# Revit family: Emergency_Equipment-Tepid-Floor_Mounted_Eye_Face_Wash-S2510
name_source: partatom
category: Plumbing Fixtures
revit_build: Autodesk Revit Architecture 2016 (Build: 20150220_1215(x64)
units: mm (PartAtom-declared; Revit-internal decimal feet)

## family parameters
Always vertical = Yes
Cut with Voids When Loaded = No
OmniClass Number = 23.45.05.14.24
OmniClass Title = Eye Wash Fountains
Part Type = Normal
Room Calculation Point = No
Round Connector Dimension = Use Diameter
Shared = No
Work Plane-Based = No

## types (12) — shared parameters
C Pipe length = 0' - 1 3/4"
CW Connection = Yes
Description = Floor Mounted Eye-Face Wash
Dimension Disclaimer = Dimensions are ±0.50”. Design and specifications are subject to change without notice.
Drain Connection = 1"
HW Connection = Yes
Height = 3' - 2 5/16"
Length = 1' - 8 1/2"
Manufacturer = Stingray Systems
Product Documentation Link = http://www.tepid.com
Product Name = Floor Mounted Standard Eye-Face Wash
Product Page URL = http://www.tepid.com
Supply Connection = 1"
URL = www.tepid.com
Vent Connection = No
Version = 2016-v1.0a
Waste Connection = Yes

## per-type parameters (varying)
| type | AB Bowl | Base Finish | Bowl Material | Filter | Pipe Finish | SS Bowl | Width |
| S2510-SS-NFT-SSNA | No | Metal - Stingray - Stainless Steel SS | Metal - Stingray - Stainless Steel SS | No | Metal - Stingray - Stainless Steel SS | Yes | 1' - 2 5/16" |
| S2510-SS-NFT-ABNA | Yes | Metal - Stingray - Stainless Steel SS | Plastic - Stingray - ABS AB | No | Metal - Stingray - Stainless Steel SS | No | 1' - 4 5/16" |
| S2510-EP-NFT-SSNA | No | Metal - Stingray - Epoxy Coated EP | Metal - Stingray - Stainless Steel SS | No | Metal - Stingray - Epoxy Coated EP | Yes | 1' - 2 5/16" |
| S2510-EP-NFT-ABNA | Yes | Metal - Stingray - Epoxy Coated EP | Plastic - Stingray - ABS AB | No | Metal - Stingray - Epoxy Coated EP | No | 1' - 4 5/16" |
| S2510-GA-NFT-SSNA | No | Metal - Stingray - Epoxy Coated EP | Metal - Stingray - Stainless Steel SS | No | Metal - Stingray - Galvanized GA | Yes | 1' - 2 5/16" |
| S2510-GA-NFT-ABNA | Yes | Metal - Stingray - Epoxy Coated EP | Plastic - Stingray - ABS AB | No | Metal - Stingray - Galvanized GA | No | 1' - 4 5/16" |
| S2510-EP-FLT-ABNA | Yes | Metal - Stingray - Epoxy Coated EP | Plastic - Stingray - ABS AB | Yes | Metal - Stingray - Epoxy Coated EP | No | 1' - 4 5/16" |
| S2510-EP-FLT-SSNA | No | Metal - Stingray - Epoxy Coated EP | Metal - Stingray - Stainless Steel SS | Yes | Metal - Stingray - Epoxy Coated EP | Yes | 1' - 2 5/16" |
| S2510-GA-FLT-ABNA | Yes | Metal - Stingray - Epoxy Coated EP | Plastic - Stingray - ABS AB | Yes | Metal - Stingray - Galvanized GA | No | 1' - 4 5/16" |
| S2510-GA-FLT-SSNA | No | Metal - Stingray - Epoxy Coated EP | Metal - Stingray - Stainless Steel SS | Yes | Metal - Stingray - Galvanized GA | Yes | 1' - 2 5/16" |
| S2510-SS-FLT-ABNA | Yes | Metal - Stingray - Stainless Steel SS | Plastic - Stingray - ABS AB | Yes | Metal - Stingray - Stainless Steel SS | No | 1' - 4 5/16" |
| S2510-SS-FLT-SSNA | No | Metal - Stingray - Stainless Steel SS | Metal - Stingray - Stainless Steel SS | Yes | Metal - Stingray - Stainless Steel SS | Yes | 1' - 2 5/16" |

note: column(s) folded — value = type name in every type: Model

## geometry (parser evidence)
native form markers: Sweep x9
no freeform markers — native parametric forms only
